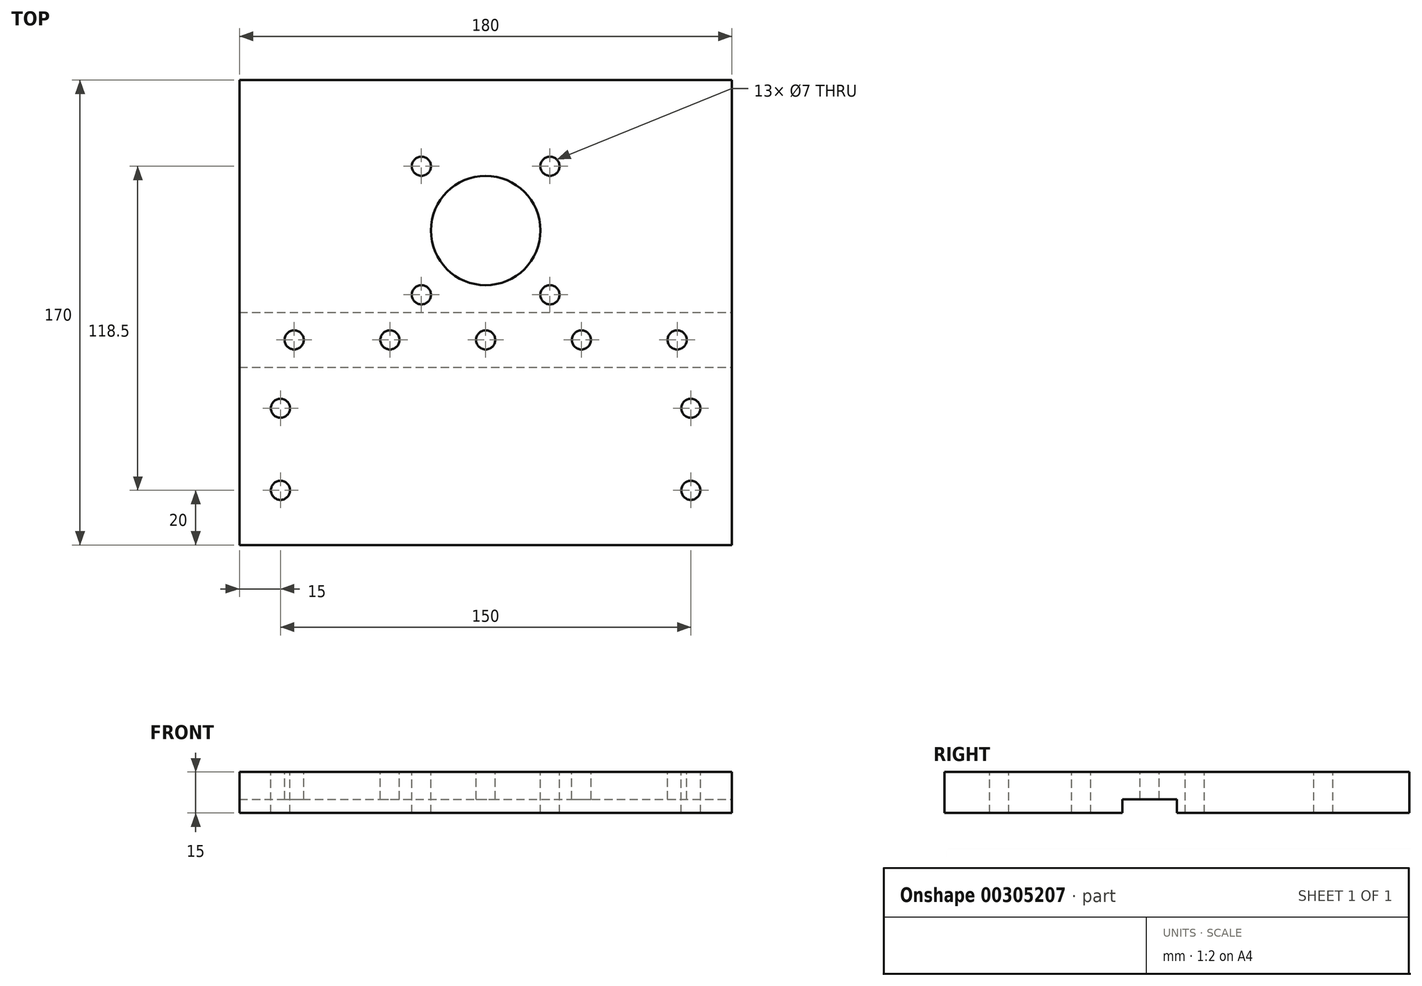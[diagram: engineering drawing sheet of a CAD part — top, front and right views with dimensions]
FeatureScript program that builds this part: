
annotation { "Feature Type Name" : "Feature", "Feature Type Description" : "" }
export const myFeature = defineFeature(function(context is Context, id is Id, definition is map)
    precondition{}
    {
        {
            var Q0;
            Q0=qCreatedBy(makeId("Front.planeOp"),FACE);
            var sketch = newSketch(context, id + "F0", { "sketchPlane" : qUnion([Q0])});
            skLineSegment(sketch, "E0.bottom", {"start": v(0, 0) * mm, "end": v(170, 0) * mm});
            skLineSegment(sketch, "E0.top", {"start": v(0, 15) * mm, "end": v(170, 15) * mm});
            skLineSegment(sketch, "E0.left", {"start": v(0, 0) * mm, "end": v(0, 15) * mm});
            skLineSegment(sketch, "E0.right", {"start": v(170, 0) * mm, "end": v(170, 15) * mm});
            skSolve(sketch);
        }
        {
            var Q0;
            Q0=makeQuery(id+"F0.imprint","IMPRINT",FACE,{"disambiguationData":[TD([[makeQuery(id+"F0.imprint","IMPRINT",EDGE,{"derivedFrom":sQuery(id+"F0.wireOp",EDGE,"E0.bottom")}),1.0]])]});
            extrude(context, id + "F1", {"entities" : qUnion([Q0]), "depth" : 150 * mm});
        }
        {
            var Q0;
            Q0=makeQuery(id+"F1.opExtrude","SWEPT_FACE",FACE,{"disambiguationData":[OSD([sQuery(id+"F0.wireOp",EDGE,"E0.bottom")])]});
            var sketch = newSketch(context, id + "F2", { "sketchPlane" : qUnion([Q0])});
            skLineSegment(sketch, "E1.bottom", {"start": v(0, 105) * mm, "end": v(170, 105) * mm});
            skLineSegment(sketch, "E1.top", {"start": v(0, 85) * mm, "end": v(170, 85) * mm});
            skLineSegment(sketch, "E1.left", {"start": v(0, 105) * mm, "end": v(0, 85) * mm});
            skLineSegment(sketch, "E1.right", {"start": v(170, 105) * mm, "end": v(170, 85) * mm});
            skSolve(sketch);
        }
        {
            var Q0;
            Q0=makeQuery(id+"F2.imprint","IMPRINT",FACE,{"disambiguationData":[TD([[makeQuery(id+"F2.imprint","IMPRINT",EDGE,{"derivedFrom":sQuery(id+"F2.wireOp",EDGE,"E1.bottom")}),-1.0]])]});
            extrude(context, id + "F3", {"entities" : qUnion([Q0]), "operationType" : NewBodyOperationType.REMOVE, "oppositeDirection" : true, "depth" : 5 * mm});
        }
        {
            var Q0;
            Q0=makeQuery(id+"F1.opExtrude","SWEPT_FACE",FACE,{"disambiguationData":[OSD([sQuery(id+"F0.wireOp",EDGE,"E0.top")])]});
            var sketch = newSketch(context, id + "F4", { "sketchPlane" : qUnion([Q0])});
            skCircle(sketch, "E2", {"center": v(85, -55) * mm, "radius": 20 * mm});
            skSolve(sketch);
        }
        {
            var Q0;
            Q0=makeQuery(id+"F4.imprint","IMPRINT",FACE,{"disambiguationData":[TD([[makeQuery(id+"F4.imprint","IMPRINT",EDGE,{"derivedFrom":sQuery(id+"F4.wireOp",EDGE,"E2")}),1.0]])]});
            extrude(context, id + "F5", {"entities" : qUnion([Q0]), "operationType" : NewBodyOperationType.REMOVE, "oppositeDirection" : true, "depth" : 25 * mm});
        }
        {
            var Q0;
            Q0=makeQuery(id+"F1.opExtrude","SWEPT_FACE",FACE,{"disambiguationData":[OSD([sQuery(id+"F0.wireOp",EDGE,"E0.top")])]});
            var sketch = newSketch(context, id + "F6", { "sketchPlane" : qUnion([Q0])});
            skPoint(sketch, "E3", {"position": v(61.5, -31.5) * mm});
            skPoint(sketch, "E4", {"position": v(108.5, -31.5) * mm});
            skPoint(sketch, "E5", {"position": v(108.5, -78.5) * mm});
            skPoint(sketch, "E6", {"position": v(61.5, -78.5) * mm});
            skSolve(sketch);
        }
        {
            var Q0;
            Q0=sQuery(id+"F6.wireOp",VERTEX,"E3");
            var Q1;
            Q1=sQuery(id+"F6.wireOp",VERTEX,"E6");
            var Q2;
            Q2=sQuery(id+"F6.wireOp",VERTEX,"E5");
            var Q3;
            Q3=sQuery(id+"F6.wireOp",VERTEX,"E4");
            var Q4;
            Q4=makeQuery(id+"F1.opExtrude","SWEPT_BODY",BODY,{"disambiguationData":[OSD([sQuery(id+"F0.wireOp",EDGE,"E0.bottom"),sQuery(id+"F0.wireOp",EDGE,"E0.top"),sQuery(id+"F0.wireOp",EDGE,"E0.left"),sQuery(id+"F0.wireOp",EDGE,"E0.right")])]});
            hole(context, id + "F7", {"style" : HoleStyle.SIMPLE, "endStyle" : HoleEndStyle.THROUGH, "holeDiameter" : 7 * mm, "tappedDepth" : 12.6 * mm, "tapClearance" : 3, "startFromSketch" : true, "locations" : qUnion([Q0, Q1, Q2, Q3]), "scope" : qUnion([Q4])});
        }
        {
            var Q0;
            Q0=makeQuery(id+"F1.opExtrude","SWEPT_FACE",FACE,{"disambiguationData":[OSD([sQuery(id+"F0.wireOp",EDGE,"E0.left")])]});
            extrude(context, id + "F8", {"entities" : qUnion([Q0]), "operationType" : NewBodyOperationType.ADD, "depth" : 5 * mm});
        }
        {
            var Q0;
            Q0=makeQuery(id+"F1.opExtrude","SWEPT_FACE",FACE,{"disambiguationData":[OSD([sQuery(id+"F0.wireOp",EDGE,"E0.right")])]});
            extrude(context, id + "F9", {"entities" : qUnion([Q0]), "operationType" : NewBodyOperationType.ADD, "depth" : 5 * mm});
        }
        {
            var Q0;
            {var subQ0=sQuery(id+"F0.wireOp",EDGE,"E0.top");Q0=makeQuery(id+"F9.boolean.opBoolean","MERGE",FACE,{"derivedFrom":[makeQuery(id+"F8.boolean.opBoolean","MERGE",FACE,{"derivedFrom":[makeQuery(id+"F1.opExtrude","SWEPT_FACE",FACE,{"disambiguationData":[OSD([subQ0])]}),makeQuery(id+"F8.opExtrude","SWEPT_FACE",FACE,{"disambiguationData":[OSD([subQ0,sQuery(id+"F0.wireOp",EDGE,"E0.left")])]})]}),makeQuery(id+"F9.opExtrude","SWEPT_FACE",FACE,{"disambiguationData":[OSD([subQ0,sQuery(id+"F0.wireOp",EDGE,"E0.right")])]})]});}
            var sketch = newSketch(context, id + "F10", { "sketchPlane" : qUnion([Q0])});
            skPoint(sketch, "E7", {"position": v(15, -95) * mm});
            skPoint(sketch, "E8", {"position": v(50, -95) * mm});
            skPoint(sketch, "E9", {"position": v(85, -95) * mm});
            skPoint(sketch, "E10", {"position": v(120, -95) * mm});
            skPoint(sketch, "E11", {"position": v(155, -95) * mm});
            skSolve(sketch);
        }
        {
            var Q0;
            Q0=sQuery(id+"F10.wireOp",VERTEX,"E8");
            var Q1;
            Q1=sQuery(id+"F10.wireOp",VERTEX,"E7");
            var Q2;
            Q2=sQuery(id+"F10.wireOp",VERTEX,"E9");
            var Q3;
            Q3=sQuery(id+"F10.wireOp",VERTEX,"E10");
            var Q4;
            Q4=sQuery(id+"F10.wireOp",VERTEX,"E11");
            var Q5;
            Q5=makeQuery(id+"F1.opExtrude","SWEPT_BODY",BODY,{"disambiguationData":[OSD([sQuery(id+"F0.wireOp",EDGE,"E0.bottom"),sQuery(id+"F0.wireOp",EDGE,"E0.top"),sQuery(id+"F0.wireOp",EDGE,"E0.left"),sQuery(id+"F0.wireOp",EDGE,"E0.right")])]});
            hole(context, id + "F11", {"style" : HoleStyle.SIMPLE, "endStyle" : HoleEndStyle.THROUGH, "holeDiameter" : 7 * mm, "isTappedThrough" : true, "tappedDepth" : 21 * mm, "tapClearance" : 3, "startFromSketch" : true, "locations" : qUnion([Q0, Q1, Q2, Q3, Q4]), "scope" : qUnion([Q5])});
        }
        {
            var Q0;
            {var subQ0=sQuery(id+"F0.wireOp",EDGE,"E0.top");Q0=makeQuery(id+"F9.boolean.opBoolean","MERGE",FACE,{"derivedFrom":[makeQuery(id+"F8.boolean.opBoolean","MERGE",FACE,{"derivedFrom":[makeQuery(id+"F1.opExtrude","SWEPT_FACE",FACE,{"disambiguationData":[OSD([subQ0])]}),makeQuery(id+"F8.opExtrude","SWEPT_FACE",FACE,{"disambiguationData":[OSD([subQ0,sQuery(id+"F0.wireOp",EDGE,"E0.left")])]})]}),makeQuery(id+"F9.opExtrude","SWEPT_FACE",FACE,{"disambiguationData":[OSD([subQ0,sQuery(id+"F0.wireOp",EDGE,"E0.right")])]})]});}
            var sketch = newSketch(context, id + "F12", { "sketchPlane" : qUnion([Q0])});
            skPoint(sketch, "E12", {"position": v(160, -120) * mm});
            skPoint(sketch, "E13", {"position": v(10, -120) * mm});
            skSolve(sketch);
        }
        {
            var Q0;
            Q0=sQuery(id+"F12.wireOp",VERTEX,"E13");
            var Q1;
            Q1=sQuery(id+"F12.wireOp",VERTEX,"6072ab0d-fc2a-4d4f-8d3d-b976371cbb0b");
            var Q2;
            Q2=sQuery(id+"F12.wireOp",VERTEX,"E12");
            var Q3;
            Q3=sQuery(id+"F12.wireOp",VERTEX,"71eb552f-1239-433a-b292-925cb35658aa");
            var Q4;
            Q4=makeQuery(id+"F1.opExtrude","SWEPT_BODY",BODY,{"disambiguationData":[OSD([sQuery(id+"F0.wireOp",EDGE,"E0.bottom"),sQuery(id+"F0.wireOp",EDGE,"E0.top"),sQuery(id+"F0.wireOp",EDGE,"E0.left"),sQuery(id+"F0.wireOp",EDGE,"E0.right")])]});
            hole(context, id + "F13", {"style" : HoleStyle.SIMPLE, "endStyle" : HoleEndStyle.THROUGH, "holeDiameter" : 7 * mm, "isTappedThrough" : true, "tappedDepth" : 21 * mm, "tapClearance" : 3, "startFromSketch" : true, "locations" : qUnion([Q0, Q1, Q2, Q3]), "scope" : qUnion([Q4])});
        }
        {
            var Q0;
            {var subQ0=sQuery(id+"F0.wireOp",EDGE,"E0.right");var subQ1=sQuery(id+"F0.wireOp",EDGE,"E0.left");Q0=makeQuery(id+"F9.boolean.opBoolean","MERGE",FACE,{"derivedFrom":[makeQuery(id+"F8.boolean.opBoolean","MERGE",FACE,{"derivedFrom":[makeQuery(id+"F1.opExtrude","CAP_FACE",FACE,{"disambiguationData":[OSD([sQuery(id+"F0.wireOp",EDGE,"E0.bottom"),sQuery(id+"F0.wireOp",EDGE,"E0.top"),subQ1,subQ0])],"isStart":false}),makeQuery(id+"F8.opExtrude","SWEPT_FACE",FACE,{"disambiguationData":[OSD([subQ1]),TDD([makeQuery(id+"F1.opExtrude","CAP_EDGE",EDGE,{"disambiguationData":[OSD([subQ1])],"isStart":false})])]})]}),makeQuery(id+"F9.opExtrude","SWEPT_FACE",FACE,{"disambiguationData":[OSD([subQ0]),TDD([makeQuery(id+"F1.opExtrude","CAP_EDGE",EDGE,{"disambiguationData":[OSD([subQ0])],"isStart":false})])]})]});}
            extrude(context, id + "F14", {"entities" : qUnion([Q0]), "operationType" : NewBodyOperationType.ADD, "depth" : 20 * mm});
        }
        {
            var Q0;
            {var subQ0=sQuery(id+"F0.wireOp",EDGE,"E0.right");var subQ1=sQuery(id+"F0.wireOp",EDGE,"E0.left");var subQ2=sQuery(id+"F0.wireOp",EDGE,"E0.top");Q0=makeQuery(id+"F14.boolean.opBoolean","MERGE",FACE,{"derivedFrom":[makeQuery(id+"F9.boolean.opBoolean","MERGE",FACE,{"derivedFrom":[makeQuery(id+"F8.boolean.opBoolean","MERGE",FACE,{"derivedFrom":[makeQuery(id+"F1.opExtrude","SWEPT_FACE",FACE,{"disambiguationData":[OSD([subQ2])]}),makeQuery(id+"F8.opExtrude","SWEPT_FACE",FACE,{"disambiguationData":[OSD([subQ2,subQ1])]})]}),makeQuery(id+"F9.opExtrude","SWEPT_FACE",FACE,{"disambiguationData":[OSD([subQ2,subQ0])]})]}),makeQuery(id+"F14.opExtrude","SWEPT_FACE",FACE,{"disambiguationData":[OSD([subQ2,subQ1,subQ0])]})]});}
            var sketch = newSketch(context, id + "F15", { "sketchPlane" : qUnion([Q0])});
            skPoint(sketch, "E14", {"position": v(10, -150) * mm});
            skPoint(sketch, "E15", {"position": v(160, -150) * mm});
            skPoint(sketch, "E16", {"position": v(10, -120) * mm});
            skSolve(sketch);
        }
        {
            var Q0;
            Q0=sQuery(id+"F15.wireOp",VERTEX,"E14");
            var Q1;
            Q1=sQuery(id+"F15.wireOp",VERTEX,"E15");
            var Q2;
            Q2=makeQuery(id+"F1.opExtrude","SWEPT_BODY",BODY,{"disambiguationData":[OSD([sQuery(id+"F0.wireOp",EDGE,"E0.bottom"),sQuery(id+"F0.wireOp",EDGE,"E0.top"),sQuery(id+"F0.wireOp",EDGE,"E0.left"),sQuery(id+"F0.wireOp",EDGE,"E0.right")])]});
            hole(context, id + "F16", {"style" : HoleStyle.SIMPLE, "endStyle" : HoleEndStyle.THROUGH, "holeDiameter" : 7 * mm, "isTappedThrough" : true, "tappedDepth" : 21 * mm, "tapClearance" : 3, "startFromSketch" : true, "locations" : qUnion([Q0, Q1]), "scope" : qUnion([Q2])});
        }
    });
